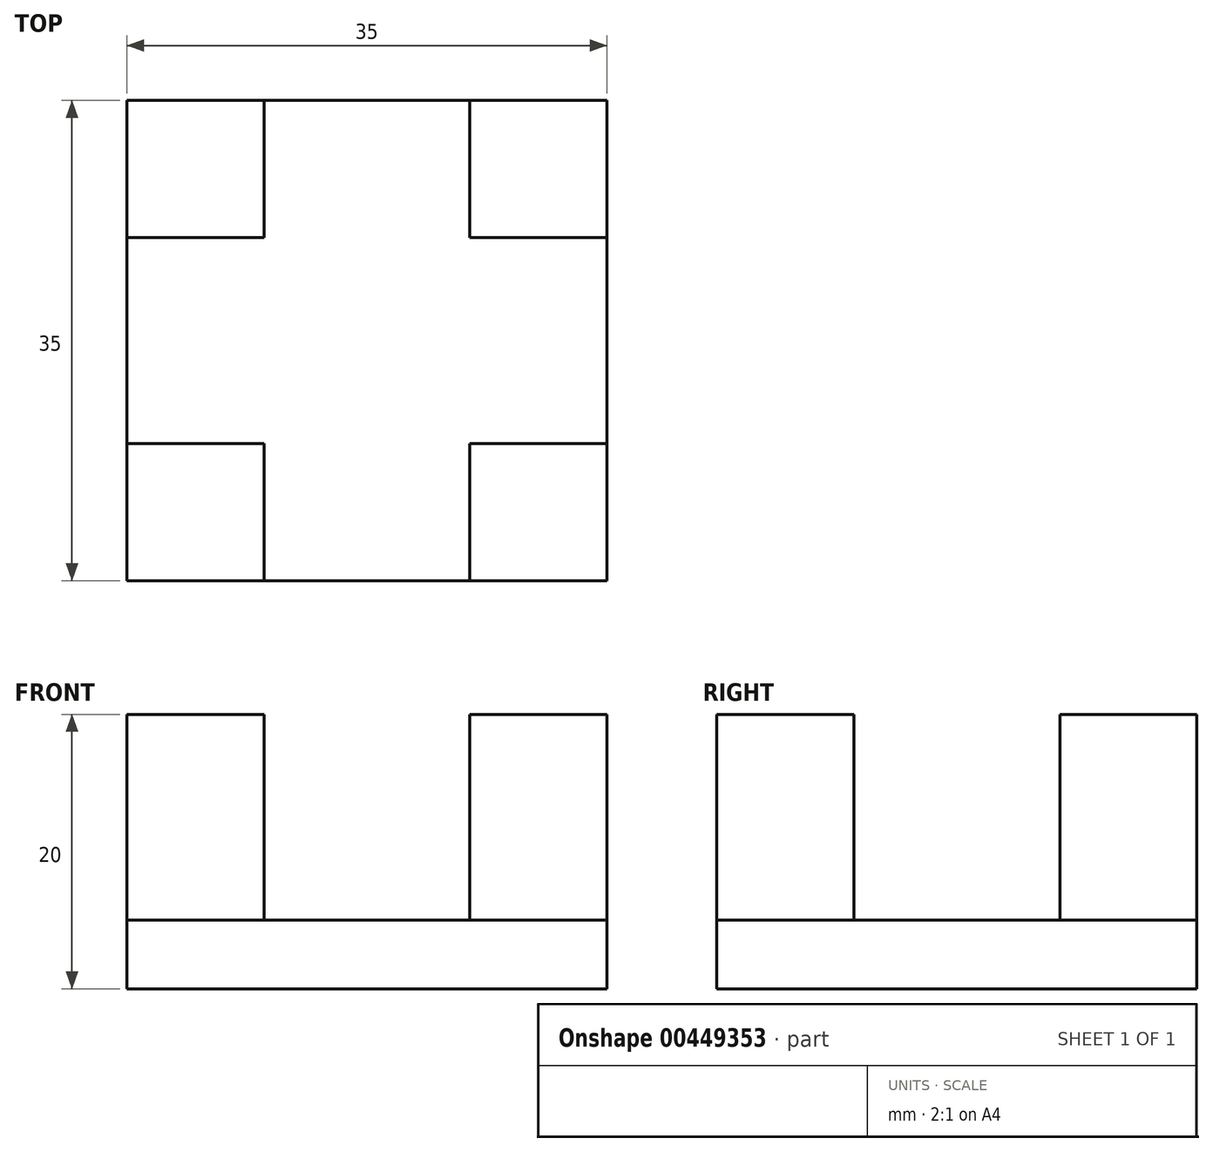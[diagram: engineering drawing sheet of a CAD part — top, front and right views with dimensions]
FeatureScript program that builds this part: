
annotation { "Feature Type Name" : "Feature", "Feature Type Description" : "" }
export const myFeature = defineFeature(function(context is Context, id is Id, definition is map)
    precondition{}
    {
        {
            var Q0;
            Q0=qCreatedBy(makeId("Top.planeOp"),FACE);
            var sketch = newSketch(context, id + "F0", { "sketchPlane" : qUnion([Q0])});
            skLineSegment(sketch, "E0.bottom", {"start": v(5, 5) * mm, "end": v(15, 5) * mm});
            skLineSegment(sketch, "E0.top", {"start": v(5, 15) * mm, "end": v(15, 15) * mm});
            skLineSegment(sketch, "E0.left", {"start": v(5, 5) * mm, "end": v(5, 15) * mm});
            skLineSegment(sketch, "E0.right", {"start": v(15, 5) * mm, "end": v(15, 15) * mm});
            skLineSegment(sketch, "E1.0.1.0", {"start": v(5, 40) * mm, "end": v(15, 40) * mm});
            skLineSegment(sketch, "E1.0.1.1", {"start": v(15, 30) * mm, "end": v(15, 40) * mm});
            skLineSegment(sketch, "E1.0.1.2", {"start": v(5, 30) * mm, "end": v(15, 30) * mm});
            skLineSegment(sketch, "E1.0.1.3", {"start": v(5, 30) * mm, "end": v(5, 40) * mm});
            skLineSegment(sketch, "E1.1.0.0", {"start": v(30, 15) * mm, "end": v(40, 15) * mm});
            skLineSegment(sketch, "E1.1.0.1", {"start": v(40, 5) * mm, "end": v(40, 15) * mm});
            skLineSegment(sketch, "E1.1.0.2", {"start": v(30, 5) * mm, "end": v(40, 5) * mm});
            skLineSegment(sketch, "E1.1.0.3", {"start": v(30, 5) * mm, "end": v(30, 15) * mm});
            skLineSegment(sketch, "E1.1.1.0", {"start": v(30, 40) * mm, "end": v(40, 40) * mm});
            skLineSegment(sketch, "E1.1.1.1", {"start": v(40, 30) * mm, "end": v(40, 40) * mm});
            skLineSegment(sketch, "E1.1.1.2", {"start": v(30, 30) * mm, "end": v(40, 30) * mm});
            skLineSegment(sketch, "E1.1.1.3", {"start": v(30, 30) * mm, "end": v(30, 40) * mm});
            skLineSegment(sketch, "E1.direction1", {"start": v(5, 15) * mm, "end": v(30, 15) * mm, "construction": true});
            skLineSegment(sketch, "E2.bottom", {"start": v(40, 40) * mm, "end": v(5, 40) * mm});
            skLineSegment(sketch, "E2.top", {"start": v(40, 5) * mm, "end": v(5, 5) * mm});
            skLineSegment(sketch, "E2.left", {"start": v(40, 40) * mm, "end": v(40, 5) * mm});
            skLineSegment(sketch, "E2.right", {"start": v(5, 40) * mm, "end": v(5, 5) * mm});
            skSolve(sketch);
        }
        {
            var Q0;
            {var subQ0=sQuery(id+"F0.wireOp",EDGE,"E1.1.0.0");Q0=makeQuery(id+"F0.imprint","IMPRINT",FACE,{"disambiguationData":[TD([[makeQuery(id+"F0.imprint","IMPRINT",EDGE,{"derivedFrom":subQ0}),-1.0]])]});}
            var Q1;
            {var subQ0=sQuery(id+"F0.wireOp",EDGE,"E0.top");Q1=makeQuery(id+"F0.imprint","IMPRINT",FACE,{"disambiguationData":[TD([[makeQuery(id+"F0.imprint","IMPRINT",EDGE,{"derivedFrom":subQ0}),-1.0]])]});}
            var Q2;
            {var subQ0=sQuery(id+"F0.wireOp",EDGE,"E1.0.1.1");Q2=makeQuery(id+"F0.imprint","IMPRINT",FACE,{"disambiguationData":[TD([[makeQuery(id+"F0.imprint","IMPRINT",EDGE,{"derivedFrom":subQ0}),1.0]])]});}
            var Q3;
            {var subQ0=sQuery(id+"F0.wireOp",EDGE,"E1.1.1.2");Q3=makeQuery(id+"F0.imprint","IMPRINT",FACE,{"disambiguationData":[TD([[makeQuery(id+"F0.imprint","IMPRINT",EDGE,{"derivedFrom":subQ0}),1.0]])]});}
            extrude(context, id + "F1", {"entities" : qUnion([Q0, Q1, Q2, Q3]), "depth" : 15 * mm});
        }
        {
            var Q0;
            Q0 = qSketchRegion(id + "F0", true);
            extrude(context, id + "F2", {"entities" : qUnion([Q0]), "oppositeDirection" : true, "depth" : 5 * mm});
        }
    });
